# Revit family: ALBA_R150ExWSxx
name_source: partatom
category: Leuchten
units: mm (PartAtom-declared; Revit-internal decimal feet)

## family parameters
Basisbauteil = Fläche
Beim Laden mit Abzugskörper schneiden = Nein
Bemaßung runder Anschluss = Durchmesser verwenden
Gemeinsam genutzt = Nein
Lichtquelle = Ja
OmniClass-Nummer = 23.80.70.11
OmniClass-Titel = Luminaries for Internal Lighting
Raumberechnungspunkt = Nein
Teiletyp = Normal

## types (8) — shared parameters
Baugruppenkennzeichen = D5020200
Emissionsform beim Rendern sichtbar = Nein
Farbfilter = 16777215
Farbtemperaturverschiebung bei Dämpfen der Lampe = <Keine Auswahl>
Hersteller = RIDI Leuchten GmbH
Lampe = LED
Neigungswinkel = 90.00°
Scheinlast = 19 VA
URL = www.ridi.de
Von Kreisdurchmesser aussenden = 134 mm
brand = RIDI
conformity mark = CE
electrical safety class = 2
height = 95 mm
ingress protection (IP) code = IP20
length = 160 mm  [stored 0.524934 ft]
nominal frequency = 50-60Hz
nominal voltage = 230
rated input power = 19
voltage type (AC, DC, UC) = AC
weight = 0.65 kg
width = 160 mm  [stored 0.524934 ft]
zero-valued in all types: Vorgabe-Ansicht

## per-type parameters (varying)
| type | Datei für fotometrisches Netz | Modell |
| ALBA R150E NDWS830SF0260OS | Master_ALBA_R150E_NDMM840_Diffusor.IES | 0322133 |
| ALBA R150E NDWS840SF0260OS | Master_ALBA_R150E_NDMM840_Diffusor.IES | 0322130 |
| ALBA R150E NDWS830F0260 | Master_ALBA_R150E_NDMM840_Linse_F.IES | 0322131 |
| ALBA R150E NDWS840F0260 | Master_ALBA_R150E_NDMM840_Linse_F.IES | 0322132 |
| ALBA R150E DAWS830SF0260OS | Master_ALBA_R150E_NDMM840_Diffusor.IES | 0332129 |
| ALBA R150E DAWS840SF0260OS | Master_ALBA_R150E_NDMM840_Diffusor.IES | 0332130 |
| ALBA R150E DAWS830F0260 | Master_ALBA_R150E_NDMM840_Linse_F.IES | 0332131 |
| ALBA R150E DAWS840F0260 | Master_ALBA_R150E_NDMM840_Linse_F.IES | 0332132 |

note: column(s) folded — value = type name in every type: product name

note: [stored X ft] marks values corroborated as IEEE doubles in the binary element streams (Revit-internal decimal feet)
